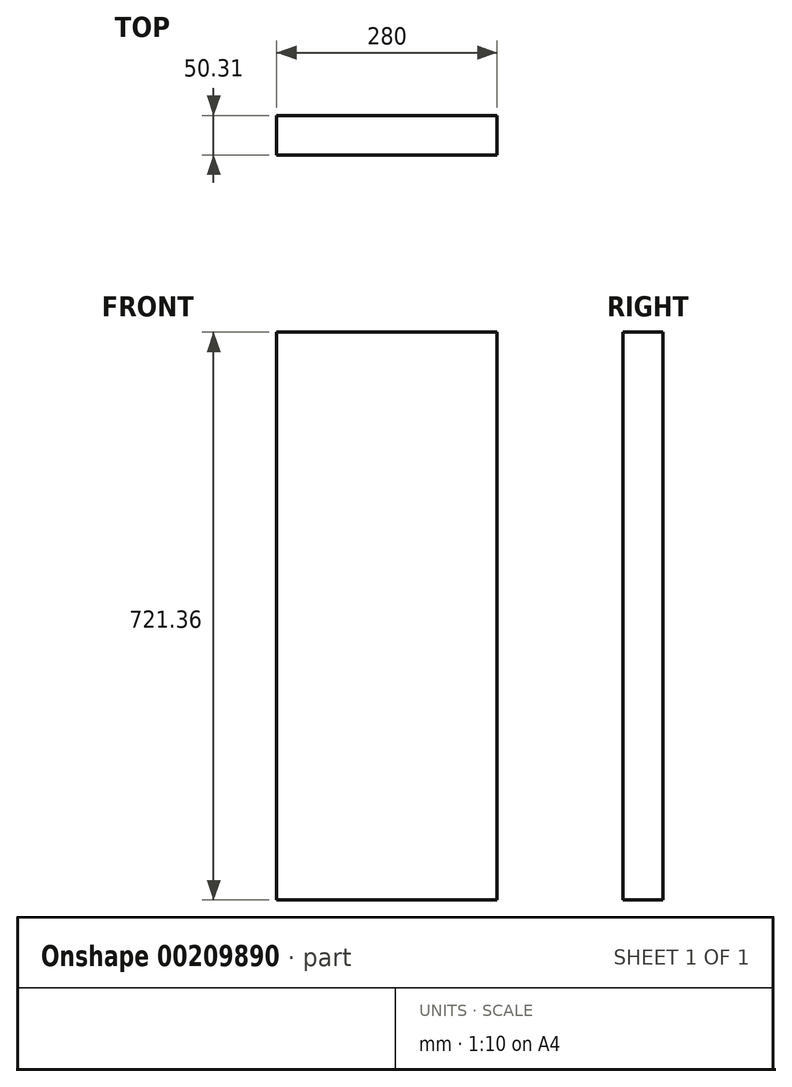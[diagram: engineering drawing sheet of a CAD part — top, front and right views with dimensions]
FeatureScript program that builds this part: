
annotation { "Feature Type Name" : "Feature", "Feature Type Description" : "" }
export const myFeature = defineFeature(function(context is Context, id is Id, definition is map)
    precondition{}
    {
        {
            var Q0;
            Q0=qCreatedBy(makeId("Right.planeOp"),FACE);
            var sketch = newSketch(context, id + "F0", { "sketchPlane" : qUnion([Q0])});
            skLineSegment(sketch, "E0.bottom", {"start": v(50.31, 60.29) * mm, "end": v(0, 60.29) * mm});
            skLineSegment(sketch, "E0.top", {"start": v(50.31, 781.65) * mm, "end": v(0, 781.65) * mm});
            skLineSegment(sketch, "E0.left", {"start": v(50.31, 60.29) * mm, "end": v(50.31, 781.65) * mm});
            skLineSegment(sketch, "E0.right", {"start": v(0, 60.29) * mm, "end": v(0, 781.65) * mm});
            skSolve(sketch);
        }
        {
            var Q0;
            Q0=makeQuery(id+"F0.imprint","IMPRINT",FACE,{"disambiguationData":[TD([[makeQuery(id+"F0.imprint","IMPRINT",EDGE,{"derivedFrom":sQuery(id+"F0.wireOp",EDGE,"E0.bottom")}),-1.0]])]});
            extrude(context, id + "F1", {"entities" : qUnion([Q0]), "depth" : 280 * mm});
        }
    });
